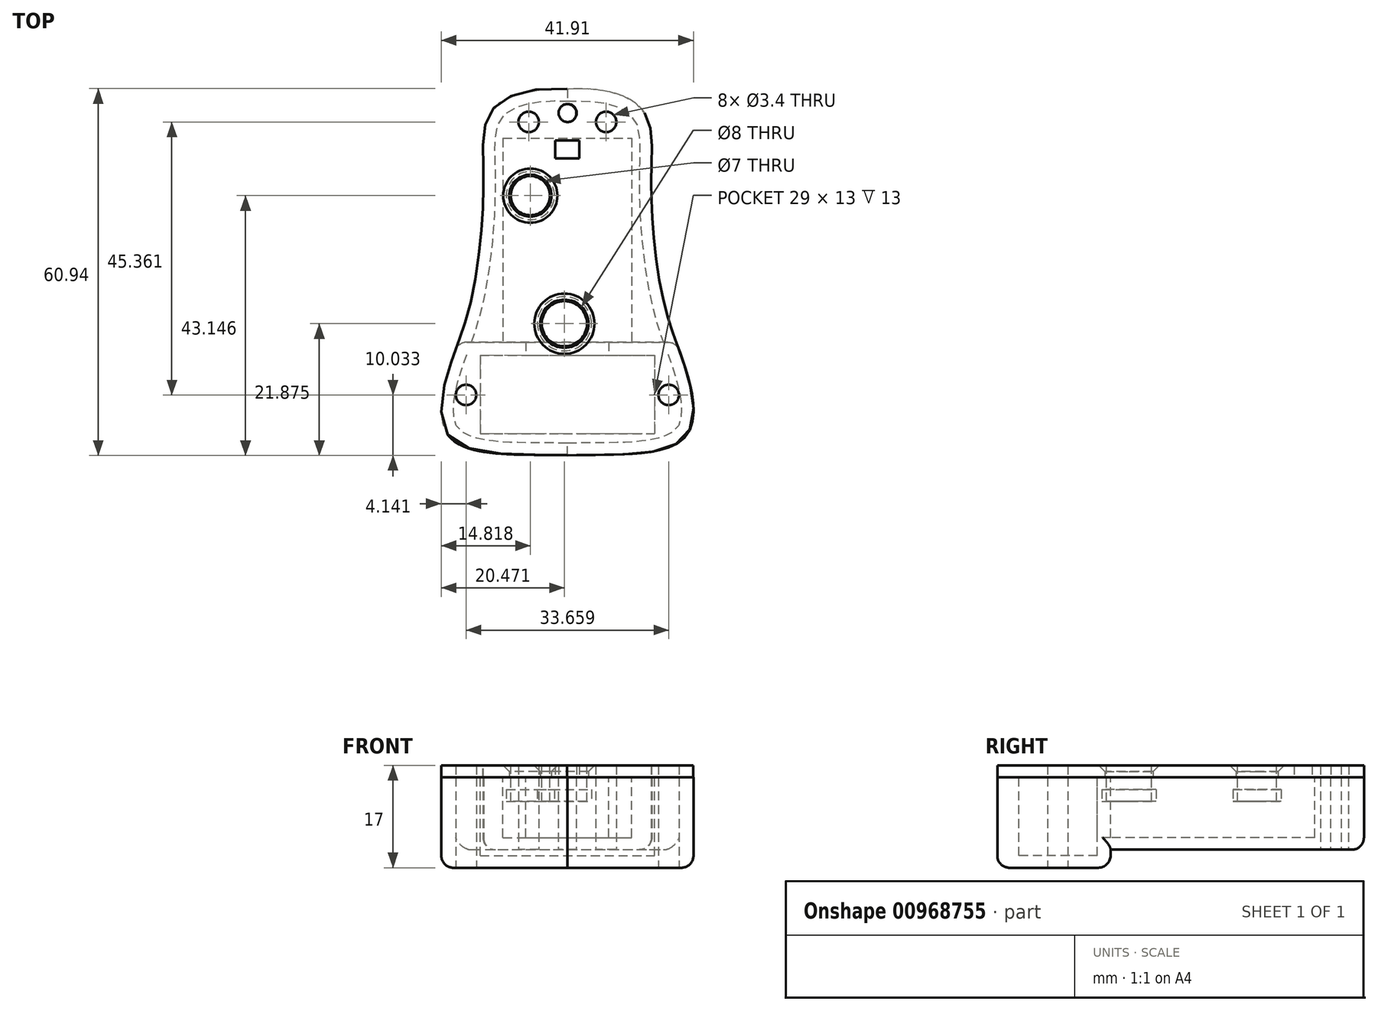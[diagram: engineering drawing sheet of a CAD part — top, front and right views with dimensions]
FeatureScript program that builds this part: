
annotation { "Feature Type Name" : "Feature", "Feature Type Description" : "" }
export const myFeature = defineFeature(function(context is Context, id is Id, definition is map)
    precondition{}
    {
        {
            assignVariable(context, id + "F0", {"name" : "Vastagsag", "anyValue" : 15});
        }
        {
            assignVariable(context, id + "F1", {"name" : "PCBdeep", "anyValue" : 10});
        }
        {
            var Q0;
            Q0=qCreatedBy(makeId("Top.planeOp"),FACE);
            var sketch = newSketch(context, id + "F2", { "sketchPlane" : qUnion([Q0])});
            skLineSegment(sketch, "E0.bottom", {"start": v(-14.5, -2.19) * mm, "end": v(14.5, -2.19) * mm});
            skLineSegment(sketch, "E0.top", {"start": v(-14.5, -15.19) * mm, "end": v(14.5, -15.19) * mm});
            skLineSegment(sketch, "E0.left", {"start": v(-14.5, -2.19) * mm, "end": v(-14.5, -15.19) * mm});
            skLineSegment(sketch, "E0.right", {"start": v(14.5, -2.19) * mm, "end": v(14.5, -15.19) * mm});
            skFitSpline(sketch, "E1", {"points": [v(0, -18.8) * mm, v(-19.8, -15.47) * mm, v(-19.16, -2.96) * mm, v(-18.07, 0) * mm, v(-15.9, 7.09) * mm, v(-14.17, 19.83) * mm, v(-13.97, 29.58) * mm, v(-12.69, 38.3) * mm, v(0, 42.04) * mm], "startDerivative": vector(-109.5, 5.85) * mm, "endDerivative": vector(131.64, -7.13) * mm});
            skFitSpline(sketch, "E2.MirrorCS", {"points": [v(0, -18.8) * mm, v(19.8, -15.47) * mm, v(19.16, -2.96) * mm, v(18.07, 0) * mm, v(15.9, 7.09) * mm, v(14.17, 19.83) * mm, v(13.97, 29.58) * mm, v(12.69, 38.3) * mm, v(0, 42.04) * mm], "startDerivative": vector(109.5, 5.85) * mm, "endDerivative": vector(-131.64, -7.13) * mm});
            skCircle(sketch, "E3", {"center": v(0, 38.05) * mm, "radius": 1.5 * mm});
            skPoint(sketch, "E4", {"position": v(-16.83, -8.77) * mm});
            skPoint(sketch, "E5.MirrorP", {"position": v(16.83, -8.77) * mm});
            skPoint(sketch, "E6", {"position": v(-6.43, 36.6) * mm});
            skPoint(sketch, "E7.MirrorP", {"position": v(6.43, 36.6) * mm});
            skSolve(sketch);
        }
        {
            var Q0;
            Q0 = qSketchRegion(id + "F2", true);
            var Q1;
            Q1=makeQuery(id+"F2.imprint","IMPRINT",FACE,{"disambiguationData":[TD([[makeQuery(id+"F2.imprint","IMPRINT",EDGE,{"derivedFrom":sQuery(id+"F2.wireOp",EDGE,"E0.bottom")}),-1.0]])]});
            extrude(context, id + "F3", {"entities" : qUnion([Q0, Q1]), "flatOperationType" : FlatOperationType.REMOVE, "depth" : (getVariable(context, 'Vastagsag')) * mm, "offsetDistance" : 25 * mm, "domain" : OperationDomain.MODEL});
        }
        {
            var Q0;
            Q0=makeQuery(id+"F3.opExtrude","CAP_FACE",FACE,{"disambiguationData":[OSD([sQuery(id+"F2.wireOp",EDGE,"E1"),sQuery(id+"F2.wireOp",EDGE,"E2.MirrorCS"),sQuery(id+"F2.wireOp",EDGE,"E3")])],"isStart":false});
            var sketch = newSketch(context, id + "F4", { "sketchPlane" : qUnion([Q0])});
            skLineSegment(sketch, "E8.bottom", {"start": v(-10.7, 33.9) * mm, "end": v(10.7, 33.9) * mm});
            skLineSegment(sketch, "E8.top", {"start": v(-10.7, 0) * mm, "end": v(10.7, 0) * mm});
            skLineSegment(sketch, "E8.left", {"start": v(-10.7, 33.9) * mm, "end": v(-10.7, 0) * mm});
            skLineSegment(sketch, "E8.right", {"start": v(10.7, 33.9) * mm, "end": v(10.7, 0) * mm});
            skLineSegment(sketch, "E9.bottom", {"start": v(-14.5, -2.19) * mm, "end": v(14.5, -2.19) * mm});
            skLineSegment(sketch, "E9.top", {"start": v(-14.5, -15.19) * mm, "end": v(14.5, -15.19) * mm});
            skLineSegment(sketch, "E9.left", {"start": v(-14.5, -2.19) * mm, "end": v(-14.5, -15.19) * mm});
            skLineSegment(sketch, "E9.right", {"start": v(14.5, -2.19) * mm, "end": v(14.5, -15.19) * mm});
            skLineSegment(sketch, "E10.bottom", {"start": v(-6.88, 0) * mm, "end": v(6.88, 0) * mm});
            skLineSegment(sketch, "E10.top", {"start": v(-6.88, -2.19) * mm, "end": v(6.88, -2.19) * mm});
            skLineSegment(sketch, "E10.left", {"start": v(-6.88, 0) * mm, "end": v(-6.88, -2.19) * mm});
            skLineSegment(sketch, "E10.right", {"start": v(6.88, 0) * mm, "end": v(6.88, -2.19) * mm});
            skSolve(sketch);
        }
        {
            var Q0;
            Q0=makeQuery(id+"F4.imprint","IMPRINT",FACE,{"disambiguationData":[TD([[makeQuery(id+"F4.imprint","IMPRINT",EDGE,{"derivedFrom":sQuery(id+"F4.wireOp",EDGE,"E8.bottom")}),-1.0]])]});
            var Q1;
            {var subQ0=sQuery(id+"F4.wireOp",EDGE,"E10.left");Q1=makeQuery(id+"F4.imprint","IMPRINT",FACE,{"disambiguationData":[TD([[makeQuery(id+"F4.imprint","IMPRINT",EDGE,{"derivedFrom":subQ0}),1.0]])]});}
            extrude(context, id + "F5", {"entities" : qUnion([Q0, Q1]), "operationType" : NewBodyOperationType.REMOVE, "oppositeDirection" : true, "depth" : (getVariable(context, 'PCBdeep')) * mm, "offsetDistance" : 25 * mm});
        }
        {
            var Q0;
            Q0=makeQuery(id+"F4.imprint","IMPRINT",FACE,{"disambiguationData":[TD([[makeQuery(id+"F4.imprint","IMPRINT",EDGE,{"derivedFrom":sQuery(id+"F4.wireOp",EDGE,"E9.top")}),1.0]])]});
            extrude(context, id + "F6", {"entities" : qUnion([Q0]), "operationType" : NewBodyOperationType.REMOVE, "oppositeDirection" : true, "depth" : (getVariable(context, 'Vastagsag') - 2) * mm, "offsetDistance" : 25 * mm});
        }
        {
            var Q0;
            Q0=qCreatedBy(makeId("Top.planeOp"),FACE);
            var sketch = newSketch(context, id + "F7", { "sketchPlane" : qUnion([Q0])});
            skLineSegment(sketch, "E11.bottom", {"start": v(-24.04, 46.9) * mm, "end": v(23.32, 46.9) * mm});
            skLineSegment(sketch, "E11.top", {"start": v(-24.04, 0) * mm, "end": v(23.32, 0) * mm});
            skLineSegment(sketch, "E11.left", {"start": v(-24.04, 46.9) * mm, "end": v(-24.04, 0) * mm});
            skLineSegment(sketch, "E11.right", {"start": v(23.32, 46.9) * mm, "end": v(23.32, 0) * mm});
            skSolve(sketch);
        }
        {
            var Q0;
            Q0 = qSketchRegion(id + "F7", true);
            extrude(context, id + "F8", {"entities" : qUnion([Q0]), "operationType" : NewBodyOperationType.REMOVE, "depth" : (getVariable(context, 'Vastagsag') - getVariable(context, 'PCBdeep') - 2) * mm, "offsetDistance" : 25 * mm, "hasSecondDirection" : true, "secondDirectionOppositeDirection" : true, "secondDirectionDepth" : 25 * mm});
        }
        {
            var Q0;
            Q0=qCreatedBy(makeId("Top.planeOp"),FACE);
            cPlane(context, id + "F9", {"entities" : qUnion([Q0]), "cplaneType" : CPlaneType.OFFSET, "offset" : (getVariable(context, 'Vastagsag')) * mm, "width" : 150 * mm, "height" : 150 * mm});
        }
        {
            var Q0;
            Q0=qCreatedBy(id+"F9.planeOp",FACE);
            var sketch = newSketch(context, id + "F10", { "sketchPlane" : qUnion([Q0])});
            skCircle(sketch, "E12", {"center": v(0.05, 38.08) * mm, "radius": 1.5 * mm});
            skPoint(sketch, "E13", {"position": v(-16.78, -8.74) * mm});
            skPoint(sketch, "E14.MirrorP", {"position": v(16.88, -8.74) * mm});
            skPoint(sketch, "E15", {"position": v(-6.39, 36.62) * mm});
            skPoint(sketch, "E16.MirrorP", {"position": v(6.48, 36.62) * mm});
            skCircle(sketch, "E17", {"center": v(-6.15, 24.35) * mm, "radius": 3.5 * mm});
            skCircle(sketch, "E18", {"center": v(-0.5, 3.07) * mm, "radius": 4 * mm});
            skLineSegment(sketch, "E19.bottom", {"start": v(-2, 30.5) * mm, "end": v(2, 30.5) * mm});
            skLineSegment(sketch, "E19.top", {"start": v(-2, 33.5) * mm, "end": v(2, 33.5) * mm});
            skLineSegment(sketch, "E19.left", {"start": v(-2, 30.5) * mm, "end": v(-2, 33.5) * mm});
            skLineSegment(sketch, "E19.right", {"start": v(2, 30.5) * mm, "end": v(2, 33.5) * mm});
            skFitSpline(sketch, "E20", {"points": [v(-0.03, -18.76) * mm, v(-19.82, -15.43) * mm, v(-19.18, -2.91) * mm, v(-18.1, 0.04) * mm, v(-15.94, 7.13) * mm, v(-14.2, 19.88) * mm, v(-14, 29.63) * mm, v(-12.71, 38.35) * mm, v(-0.03, 42.08) * mm], "startDerivative": vector(-109.5, 5.85) * mm, "endDerivative": vector(131.64, -7.13) * mm});
            skFitSpline(sketch, "E21.MirrorCS", {"points": [v(-0.03, -18.76) * mm, v(19.76, -15.43) * mm, v(19.13, -2.91) * mm, v(18.04, 0.04) * mm, v(15.88, 7.13) * mm, v(14.14, 19.88) * mm, v(13.95, 29.63) * mm, v(12.66, 38.35) * mm, v(-0.03, 42.08) * mm], "startDerivative": vector(109.5, 5.85) * mm, "endDerivative": vector(-131.64, -7.13) * mm});
            skSolve(sketch);
        }
        {
            var Q0;
            Q0 = qSketchRegion(id + "F10", true);
            extrude(context, id + "F11", {"entities" : qUnion([Q0]), "depth" : 2 * mm, "offsetDistance" : 25 * mm});
        }
        {
            var Q0;
            Q0=makeQuery(id+"F11.opExtrude","CAP_FACE",FACE,{"disambiguationData":[OSD([sQuery(id+"F10.wireOp",EDGE,"ba35714b-b426-4a01-ae18-c3cfcc257b28"),sQuery(id+"F10.wireOp",EDGE,"26e0290d-45cb-4e89-aed8-fdc89f414c71.MirrorCS"),sQuery(id+"F10.wireOp",EDGE,"E12"),sQuery(id+"F10.wireOp",EDGE,"E17"),sQuery(id+"F10.wireOp",EDGE,"E18")])],"isStart":false});
            var sketch = newSketch(context, id + "F12", { "sketchPlane" : qUnion([Q0])});
            skCircle(sketch, "E22", {"center": v(-6.15, 24.35) * mm, "radius": 3.25 * mm});
            skCircle(sketch, "E23", {"center": v(-0.5, 3.07) * mm, "radius": 3.75 * mm});
            skSolve(sketch);
        }
        {
            var Q0;
            Q0 = qSketchRegion(id + "F12", true);
            extrude(context, id + "F13", {"entities" : qUnion([Q0]), "oppositeDirection" : true, "depth" : (getVariable(context, 'PCBdeep') - 4) * mm, "offsetDistance" : 25 * mm});
        }
        {
            var Q0;
            Q0=makeQuery(id+"F13.opExtrude","CAP_FACE",FACE,{"disambiguationData":[OSD([sQuery(id+"F12.wireOp",EDGE,"E23")])],"isStart":false});
            var sketch = newSketch(context, id + "F14", { "sketchPlane" : qUnion([Q0])});
            skCircle(sketch, "E24", {"center": v(-0.5, -3.07) * mm, "radius": 4.5 * mm});
            skSolve(sketch);
        }
        {
            var Q0;
            Q0=makeQuery(id+"F13.opExtrude","CAP_FACE",FACE,{"disambiguationData":[OSD([sQuery(id+"F12.wireOp",EDGE,"E22")])],"isStart":false});
            var sketch = newSketch(context, id + "F15", { "sketchPlane" : qUnion([Q0])});
            skCircle(sketch, "E25", {"center": v(-6.15, -24.35) * mm, "radius": 4 * mm});
            skSolve(sketch);
        }
        {
            var Q0;
            Q0 = qSketchRegion(id + "F14", true);
            var Q1;
            Q1 = qSketchRegion(id + "F15", true);
            extrude(context, id + "F16", {"entities" : qUnion([Q0, Q1]), "oppositeDirection" : true, "depth" : 2 * mm, "offsetDistance" : 25 * mm});
        }
        {
            var Q0;
            Q0=makeQuery(id+"F11.opExtrude","CAP_EDGE",EDGE,{"disambiguationData":[OSD([sQuery(id+"F10.wireOp",EDGE,"E17")])],"isStart":false});
            var Q1;
            Q1=makeQuery(id+"F11.opExtrude","CAP_EDGE",EDGE,{"disambiguationData":[OSD([sQuery(id+"F10.wireOp",EDGE,"E18")])],"isStart":false});
            chamfer(context, id + "F17", {"entities" : qUnion([Q0, Q1]), "width" : 1 * mm, "tangentPropagation" : true});
        }
        {
            var Q0;
            Q0=makeQuery(id+"F11.opExtrude","CAP_EDGE",EDGE,{"disambiguationData":[OSD([sQuery(id+"F10.wireOp",EDGE,"267b68ad-0e51-43aa-b755-20d2239c49d0.MirrorCS")])],"isStart":false});
            var Q1;
            Q1=makeQuery(id+"F11.opExtrude","CAP_EDGE",EDGE,{"disambiguationData":[OSD([sQuery(id+"F10.wireOp",EDGE,"4fc076bf-61b2-4f0d-9733-a1d32f7a6f2c")])],"isStart":false});
            var Q2;
            Q2=makeQuery(id+"F8.boolean.opBoolean","INTERSECT",EDGE,{"derivedFrom":[makeQuery(id+"F3.opExtrude","SWEPT_FACE",FACE,{"disambiguationData":[OSD([sQuery(id+"F2.wireOp",EDGE,"E2.MirrorCS")])]}),makeQuery(id+"F8.opExtrude","CAP_FACE",FACE,{"disambiguationData":[OSD([sQuery(id+"F7.wireOp",EDGE,"E11.bottom"),sQuery(id+"F7.wireOp",EDGE,"E11.top"),sQuery(id+"F7.wireOp",EDGE,"E11.left"),sQuery(id+"F7.wireOp",EDGE,"E11.right")])],"isStart":false})]});
            var Q3;
            Q3=makeQuery(id+"F8.boolean.opBoolean","INTERSECT",EDGE,{"derivedFrom":[makeQuery(id+"F3.opExtrude","SWEPT_FACE",FACE,{"disambiguationData":[OSD([sQuery(id+"F2.wireOp",EDGE,"E1")])]}),makeQuery(id+"F8.opExtrude","CAP_FACE",FACE,{"disambiguationData":[OSD([sQuery(id+"F7.wireOp",EDGE,"E11.bottom"),sQuery(id+"F7.wireOp",EDGE,"E11.top"),sQuery(id+"F7.wireOp",EDGE,"E11.left"),sQuery(id+"F7.wireOp",EDGE,"E11.right")])],"isStart":false})]});
            var Q4;
            Q4=makeQuery(id+"F8.boolean.opBoolean","INTERSECT",EDGE,{"derivedFrom":[makeQuery(id+"F3.opExtrude","CAP_FACE",FACE,{"disambiguationData":[OSD([sQuery(id+"F2.wireOp",EDGE,"E1"),sQuery(id+"F2.wireOp",EDGE,"E2.MirrorCS"),sQuery(id+"F2.wireOp",EDGE,"E3")])],"isStart":true}),makeQuery(id+"F8.opExtrude","SWEPT_FACE",FACE,{"disambiguationData":[OSD([sQuery(id+"F7.wireOp",EDGE,"E11.top")])]})]});
            var Q5;
            Q5=makeQuery(id+"F3.opExtrude","CAP_EDGE",EDGE,{"disambiguationData":[OSD([sQuery(id+"F2.wireOp",EDGE,"E1")])],"isStart":true});
            var Q6;
            Q6=makeQuery(id+"F3.opExtrude","CAP_EDGE",EDGE,{"disambiguationData":[OSD([sQuery(id+"F2.wireOp",EDGE,"E2.MirrorCS")])],"isStart":true});
            var Q7;
            Q7=makeQuery(id+"F8.boolean.opBoolean","INTERSECT",EDGE,{"derivedFrom":[makeQuery(id+"F3.opExtrude","SWEPT_FACE",FACE,{"disambiguationData":[OSD([sQuery(id+"F2.wireOp",EDGE,"E1")])]}),makeQuery(id+"F8.opExtrude","SWEPT_FACE",FACE,{"disambiguationData":[OSD([sQuery(id+"F7.wireOp",EDGE,"E11.top")])]})]});
            var Q8;
            Q8=makeQuery(id+"F8.boolean.opBoolean","INTERSECT",EDGE,{"derivedFrom":[makeQuery(id+"F3.opExtrude","SWEPT_FACE",FACE,{"disambiguationData":[OSD([sQuery(id+"F2.wireOp",EDGE,"E2.MirrorCS")])]}),makeQuery(id+"F8.opExtrude","SWEPT_FACE",FACE,{"disambiguationData":[OSD([sQuery(id+"F7.wireOp",EDGE,"E11.top")])]})]});
            fillet(context, id + "F18", {"entities" : qUnion([Q0, Q1, Q2, Q3, Q4, Q5, Q6, Q7, Q8]), "radius" : 2 * mm, "tangentPropagation" : true, "allowEdgeOverflow" : false});
        }
        {
            var Q0;
            Q0=sQuery(id+"F2.wireOp",VERTEX,"E4");
            var Q1;
            Q1=sQuery(id+"F2.wireOp",VERTEX,"E5.MirrorP");
            var Q2;
            Q2=sQuery(id+"F2.wireOp",VERTEX,"E7.MirrorP");
            var Q3;
            Q3=sQuery(id+"F2.wireOp",VERTEX,"E6");
            var Q4;
            Q4=makeQuery(id+"F3.opExtrude","SWEPT_BODY",BODY,{"disambiguationData":[OSD([sQuery(id+"F2.wireOp",EDGE,"E1"),sQuery(id+"F2.wireOp",EDGE,"E2.MirrorCS"),sQuery(id+"F2.wireOp",EDGE,"E3")])]});
            var Q5;
            Q5=makeQuery(id+"F11.opExtrude","SWEPT_BODY",BODY,{"disambiguationData":[OSD([sQuery(id+"F10.wireOp",EDGE,"ba35714b-b426-4a01-ae18-c3cfcc257b28"),sQuery(id+"F10.wireOp",EDGE,"26e0290d-45cb-4e89-aed8-fdc89f414c71.MirrorCS"),sQuery(id+"F10.wireOp",EDGE,"E12"),sQuery(id+"F10.wireOp",EDGE,"E17"),sQuery(id+"F10.wireOp",EDGE,"E18")])]});
            hole(context, id + "F19", {"style" : HoleStyle.SIMPLE, "endStyle" : HoleEndStyle.THROUGH, "oppositeDirection" : true, "standardTappedOrClearance" : lookupTablePath({ "fit" : "Normal", "standard" : "ISO", "size" : "M3", "type" : "Clearance" }), "standardBlindInLast" : lookupTablePath({ "fit" : "Normal", "standard" : "ISO", "engagement" : "75%", "pitch" : "0.5 mm", "size" : "M3", "type" : "Clearance & tapped" }), "holeDiameter" : 3.4 * mm, "majorDiameter" : 2 * mm, "isTappedThrough" : true, "tappedDepth" : 12 * mm, "tapClearance" : 3, "locations" : qUnion([Q0, Q1, Q2, Q3]), "scope" : qUnion([Q4, Q5])});
        }
    });
